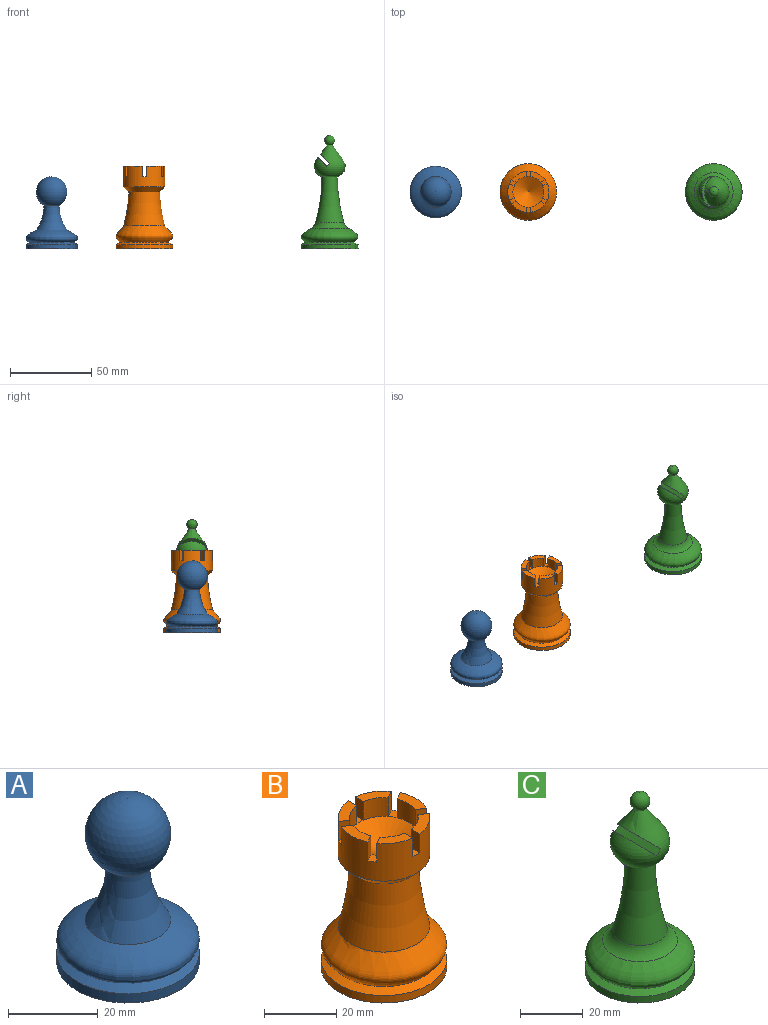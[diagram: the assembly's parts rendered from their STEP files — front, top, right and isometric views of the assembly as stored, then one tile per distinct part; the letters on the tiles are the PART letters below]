
ASSEMBLY  parts=3 mates=2
PART A: 6 faces, bbox 31.8x31.8x45.7 mm
  f0: plane 31.75x31.75mm, normal (0,0,-1), area 791.7mm2, adj f5
  f1: sphere r=9.53mm, area 1063.7mm2, adj f2
  f2: torus R=31.55mm, axis (0,0,-1), area 649.1mm2, adj f1,f3
  f3: revolved ~31.75x31.75mm, area 1060.5mm2, adj f2,f4
  f4: cone r=15.88mm half-angle=63.4deg, axis (0,0,-1), area 260.6mm2, adj f3,f5
  f5: cylinder r=15.88mm len=31.75mm, axis (0,0,-1), area 253.4mm2, adj f0,f4
PART B: 38 faces, bbox 79.2x79.2x78.9 mm
  f0: cylinder r=9.53mm len=6.35mm, axis (0,0,-1), area 47.2mm2, adj f12,f14,f22,f36
  f1: plane 9.04x6.82mm, normal (0,0,1), area 28.9mm2, adj f2,f13,f24,f33
  f2: cylinder r=12.7mm len=25.4mm, axis (0,0,-1), area 916.5mm2, adj f1,f4,f6,f8,f10,f14,f15,f20
  f3: cylinder r=9.53mm len=7.24mm, axis (0,0,-1), area 47.2mm2, adj f6,f12,f27,f34
  f4: plane 10.44x3.89mm, normal (0,0,1), area 28.9mm2, adj f2,f5,f30,f37
  f5: cylinder r=9.53mm len=7.24mm, axis (0,0,-1), area 47.2mm2, adj f4,f12,f30,f37
  f6: plane 10.44x3.89mm, normal (0,0,1), area 28.9mm2, adj f2,f3,f27,f34
  f7: cylinder r=9.53mm len=6.35mm, axis (0,0,-1), area 47.2mm2, adj f10,f12,f21,f28
  f8: plane 9.04x6.82mm, normal (0,0,1), area 28.9mm2, adj f2,f9,f23,f31
  f9: cylinder r=9.53mm len=6.35mm, axis (0,0,-1), area 47.2mm2, adj f8,f12,f23,f31
  f10: plane 9.04x6.82mm, normal (0,0,1), area 28.9mm2, adj f2,f7,f21,f28
  f11: plane 34.93x34.93mm, normal (0,0,-1), area 958mm2, adj f19
  f12: cone r=9.53mm half-angle=59deg, axis (0,0,1), area 332.5mm2, adj f0,f3,f5,f7,f9,f13,f20,f25
  f13: cylinder r=9.53mm len=6.35mm, axis (0,0,-1), area 47.2mm2, adj f1,f12,f24,f33
  f14: plane 9.04x6.82mm, normal (0,0,1), area 28.9mm2, adj f0,f2,f22,f36
  f15: cone r=12.7mm half-angle=45deg, axis (0,0,1), area 309.1mm2, adj f2,f16
  f16: torus R=102.81mm, axis (0,0,-1), area 1436.1mm2, adj f15,f17
  f17: revolved ~34.92x34.92mm, area 1257.6mm2, adj f16,f18
  f18: cone r=17.46mm half-angle=63.4deg, axis (0,0,-1), area 288.9mm2, adj f17,f19
  f19: cylinder r=17.46mm len=34.93mm, axis (0,0,-1), area 278.7mm2, adj f11,f18
  f20: plane 3.26x2.54mm, normal (0,0,1), area 8.1mm2, adj f2,f12,f21,f22
  f21: plane 6.35x3.2mm, normal (-1,0,0), area 20.3mm2, adj f2,f7,f10,f20
  f22: plane 6.35x3.2mm, normal (1,0,0), area 20.3mm2, adj f0,f2,f14,f20
  f23: plane 6.35x3.2mm, normal (1,0,0), area 20.3mm2, adj f2,f8,f9,f25
  f24: plane 6.35x3.2mm, normal (-1,0,0), area 20.3mm2, adj f1,f2,f13,f25
  f25: plane 3.26x2.54mm, normal (0,0,1), area 8.1mm2, adj f2,f12,f23,f24
  f26: plane 4.04x3.8mm, normal (0,0,1), area 8.1mm2, adj f2,f12,f27,f28
  f27: plane 6.35x2.77mm, normal (-0.5,-0.87,0), area 20.3mm2, adj f2,f3,f6,f26
  f28: plane 6.35x2.77mm, normal (0.5,0.87,0), area 20.3mm2, adj f2,f7,f10,f26
  f29: plane 4.04x3.8mm, normal (0,0,1), area 8.1mm2, adj f2,f12,f30,f31
  f30: plane 6.35x2.77mm, normal (0.5,0.87,0), area 20.3mm2, adj f2,f4,f5,f29
  f31: plane 6.35x2.77mm, normal (-0.5,-0.87,0), area 20.3mm2, adj f2,f8,f9,f29
  f32: plane 4.04x3.8mm, normal (0,0,1), area 8.1mm2, adj f2,f12,f33,f34
  f33: plane 6.35x2.77mm, normal (0.5,-0.87,0), area 20.3mm2, adj f1,f2,f13,f32
  f34: plane 6.35x2.77mm, normal (-0.5,0.87,0), area 20.3mm2, adj f2,f3,f6,f32
  f35: plane 4.04x3.8mm, normal (0,0,1), area 8.1mm2, adj f2,f12,f36,f37
  f36: plane 6.35x2.77mm, normal (-0.5,0.87,0), area 20.3mm2, adj f0,f2,f14,f35
  f37: plane 6.35x2.77mm, normal (0.5,-0.87,0), area 20.3mm2, adj f2,f4,f5,f35
PART C: 11 faces, bbox 75.6x75.6x147.7 mm
  f0: revolved ~19.5x19.04mm, area 949.7mm2, adj f2,f3,f8,f9,f10
  f1: plane 34.93x34.93mm, normal (0,0,-1), area 958mm2, adj f6
  f2: sphere r=3.17mm, area 117.7mm2, adj f0
  f3: torus R=108.79mm, axis (0,0,-1), area 1086.4mm2, adj f0,f7
  f4: revolved ~34.93x34.93mm, area 1188.7mm2, adj f5,f7
  f5: cone r=17.46mm half-angle=63.4deg, axis (0,0,-1), area 288.9mm2, adj f4,f6
  f6: cylinder r=17.46mm len=34.93mm, axis (0,0,-1), area 278.7mm2, adj f1,f5
  f7: torus R=14.76mm, axis (0,0,-1), area 336mm2, adj f3,f4
  f8: plane 18.5x5.72mm, normal (-0.71,0,-0.71), area 108.4mm2, adj f0,f10
  f9: plane 18.71x5.48mm, normal (0.71,0,0.71), area 108.3mm2, adj f0,f10
  f10: plane 18.86x1.81mm, normal (-0.71,0,0.71), area 47.6mm2, adj f0,f8,f9
PLACE A at identity
PLACE B t=(57.15,0,0)mm
PLACE C t=(171.45,0,0)mm
MATE fastened B.f0 <-> A.f0  axis (0,0,-1) through (57.15,0,0)mm
MATE fastened C.f3 <-> A.f0  axis (0,0,-1) through (171.45,0,0)mm
